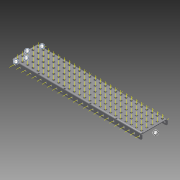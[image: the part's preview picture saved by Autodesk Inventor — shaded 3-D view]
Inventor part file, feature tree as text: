
AUTODESK INVENTOR PART (.ipt)
format: ipt  version: 2015 (Build 190159000, 159)  size: 2,755,584 bytes
history: native  units: in
note: dims shown in document units (in); Inventor stores cm internally (conversion verified against a paired STEP export)
features: other x181, pattern_linear x2, sheet_metal_op x1, extrude x1, imported_body x1, sketch x1
ambient origin geometry x8: Origin, YZ Plane, XZ Plane, XY Plane, X Axis, Y Axis, Z Axis, Center Point
bodies: Body1 (feature_tree)
feature tree (187):
  sheet_metal_op  "Fold1"
  other  "C-Channel"
  extrude  "length cut"  Depth=0.5in
  other  "top axis"
  other  "front axis"
  other  "back axis"
  pattern_linear  "top axes"  Spacing1=0.5in  [1 undecoded]
  pattern_linear  "horiz axes"  Spacing1=0.0in  [1 undecoded]
  other  "right plane"
  imported_body  "Base1"
  sketch  "Sketch1"  dims[d1=0.0in d4=0.5in d5=1.9685in d7=0.5in d10=0.5in d11=0.0in d12=0.0in d13=0.0in d14=-12.5in d15=0.0in d16=0.0in]
  other  "Work Point1"
  other  "Work Axis6"
  other  "Work Axis11"
  other  "Work Axis16"
  other  "Work Axis21"
  other  "Work Point2"
  other  "Work Point3"
  other  "Work Axis36"
  other  "Work Axis37"
  other  "Work Axis38"
  other  "Work Axis39"
  other  "Work Axis40"
  other  "Work Axis41"
  other  "Work Axis60"
  other  "Work Axis61"
  other  "Work Axis62"
  other  "Work Axis63"
  other  "Work Axis64"
  other  "Work Axis65"
  other  "Work Axis84"
  other  "Work Axis85"
  other  "Work Axis86"
  other  "Work Axis87"
  other  "Work Axis88"
  other  "Work Axis89"
  other  "Work Axis108"
  other  "Work Axis109"
  other  "Work Axis110"
  other  "Work Axis111"
  other  "Work Axis112"
  other  "Work Axis113"
  other  "Work Axis132"
  other  "Work Axis133"
  other  "Work Axis134"
  other  "Work Axis135"
  other  "Work Axis136"
  other  "Work Axis137"
  other  "Work Axis156"
  other  "Work Axis157"
  other  "Work Axis158"
  other  "Work Axis159"
  other  "Work Axis160"
  other  "Work Axis161"
  other  "Work Axis180"
  other  "Work Axis181"
  other  "Work Axis182"
  other  "Work Axis183"
  other  "Work Axis184"
  other  "Work Axis185"
  other  "Work Axis204"
  other  "Work Axis205"
  other  "Work Axis206"
  other  "Work Axis207"
  other  "Work Axis208"
  other  "Work Axis209"
  other  "Work Axis210"
  other  "Work Axis211"
  other  "Work Axis212"
  other  "Work Axis213"
  other  "Work Axis214"
  other  "Work Axis215"
  other  "Work Axis216"
  other  "Work Axis232"
  other  "Work Axis233"
  other  "Work Axis234"
  other  "Work Axis235"
  other  "Work Axis236"
  other  "Work Axis237"
  other  "Work Axis238"
  other  "Work Axis239"
  other  "Work Axis240"
  other  "Work Axis241"
  other  "Work Axis242"
  other  "Work Axis243"
  other  "Work Axis244"
  other  "Work Axis260"
  other  "Work Axis261"
  other  "Work Axis262"
  other  "Work Axis263"
  other  "Work Axis264"
  other  "Work Axis265"
  other  "Work Axis266"
  other  "Work Axis267"
  other  "Work Axis268"
  other  "Work Axis269"
  other  "Work Axis270"
  other  "Work Axis271"
  other  "Work Axis272"
  other  "Work Axis288"
  other  "Work Axis289"
  other  "Work Axis290"
  other  "Work Axis291"
  other  "Work Axis292"
  other  "Work Axis293"
  other  "Work Axis294"
  other  "Work Axis295"
  other  "Work Axis296"
  other  "Work Axis297"
  other  "Work Axis298"
  other  "Work Axis299"
  other  "Work Axis300"
  other  "Work Axis316"
  other  "Work Axis317"
  other  "Work Axis318"
  other  "Work Axis319"
  other  "Work Axis320"
  other  "Work Axis321"
  other  "Work Axis322"
  other  "Work Axis323"
  other  "Work Axis324"
  other  "Work Axis325"
  other  "Work Axis326"
  other  "Work Axis327"
  other  "Work Axis328"
  other  "Work Axis344"
  other  "Work Axis345"
  other  "Work Axis346"
  other  "Work Axis347"
  other  "Work Axis348"
  other  "Work Axis349"
  other  "Work Axis350"
  other  "Work Axis351"
  other  "Work Axis352"
  other  "Work Axis353"
  other  "Work Axis354"
  other  "Work Axis355"
  other  "Work Axis356"
  other  "Work Axis372"
  other  "Work Axis373"
  other  "Work Axis374"
  other  "Work Axis375"
  other  "Work Axis376"
  other  "Work Axis377"
  other  "Work Axis378"
  other  "Work Axis379"
  other  "Work Axis380"
  other  "Work Axis381"
  other  "Work Axis382"
  other  "Work Axis383"
  other  "Work Axis384"
  other  "left plane"
  other  "Work Axis400"
  other  "Work Axis401"
  other  "Work Axis402"
  other  "Work Axis403"
  other  "Work Axis404"
  other  "Work Axis405"
  other  "Work Axis406"
  other  "Work Axis407"
  other  "Work Axis408"
  other  "Work Axis409"
  other  "Work Axis410"
  other  "Work Axis411"
  other  "Work Axis412"
  other  "Work Axis413"
  other  "Work Axis414"
  other  "Work Axis415"
  other  "Work Axis416"
  other  "Work Axis417"
  other  "Work Axis418"
  other  "Work Axis419"
  other  "Work Axis420"
  other  "Work Axis421"
  other  "Work Axis422"
  other  "Work Axis423"
  other  "Work Axis424"
  other  "Work Axis425"
  other  "Work Axis426"
  other  "Work Axis427"
  other  "Work Axis428"
  other  "Work Axis429"
  other  "Work Axis430"
  other  "Work Axis431"
  other  "Work Axis432"
  other  "Work Axis433"
  other  "Work Axis434"
note: 2 required parameter values undecoded (feature->parameter linkage not recoverable at this tier; creation-order binding heuristic only, values carry confidence <= 0.55)
